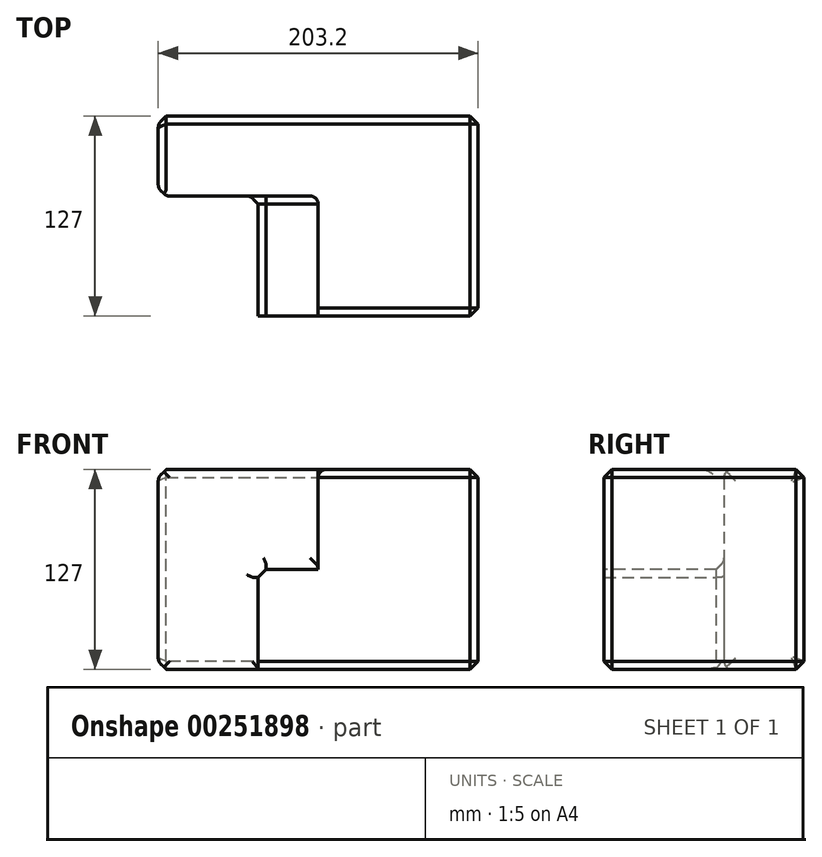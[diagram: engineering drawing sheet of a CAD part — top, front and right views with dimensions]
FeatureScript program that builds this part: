
annotation { "Feature Type Name" : "Feature", "Feature Type Description" : "" }
export const myFeature = defineFeature(function(context is Context, id is Id, definition is map)
    precondition{}
    {
        {
            var Q0;
            Q0=qCreatedBy(makeId("Front.planeOp"),FACE);
            var sketch = newSketch(context, id + "F0", { "sketchPlane" : qUnion([Q0])});
            skLineSegment(sketch, "E0.bottom", {"start": v(-101.6, 63.5) * mm, "end": v(101.6, 63.5) * mm});
            skLineSegment(sketch, "E0.top", {"start": v(-101.6, -63.5) * mm, "end": v(101.6, -63.5) * mm});
            skLineSegment(sketch, "E0.left", {"start": v(-101.6, 63.5) * mm, "end": v(-101.6, -63.5) * mm});
            skLineSegment(sketch, "E0.right", {"start": v(101.6, 63.5) * mm, "end": v(101.6, -63.5) * mm});
            skPoint(sketch, "E0.middle", {"position": v(0, 0) * mm});
            skSolve(sketch);
        }
        {
            var Q0;
            Q0 = qSketchRegion(id + "F0", true);
            extrude(context, id + "F1", {"entities" : qUnion([Q0]), "depth" : 127 * mm});
        }
        {
            var Q0;
            Q0=makeQuery(id+"F1.opExtrude","CAP_FACE",FACE,{"disambiguationData":[OSD([sQuery(id+"F0.wireOp",EDGE,"E0.bottom"),sQuery(id+"F0.wireOp",EDGE,"E0.top"),sQuery(id+"F0.wireOp",EDGE,"E0.left"),sQuery(id+"F0.wireOp",EDGE,"E0.right")])],"isStart":false});
            var sketch = newSketch(context, id + "F2", { "sketchPlane" : qUnion([Q0])});
            skLineSegment(sketch, "E1", {"start": v(-101.6, -63.5) * mm, "end": v(-101.6, 63.5) * mm});
            skLineSegment(sketch, "E2", {"start": v(-101.6, 63.5) * mm, "end": v(0, 63.5) * mm});
            skLineSegment(sketch, "E3", {"start": v(0, 63.5) * mm, "end": v(0, 0) * mm});
            skLineSegment(sketch, "E4", {"start": v(0, 0) * mm, "end": v(-38.1, 0) * mm});
            skLineSegment(sketch, "E5", {"start": v(-38.1, 0) * mm, "end": v(-38.1, -63.5) * mm});
            skLineSegment(sketch, "E6", {"start": v(-38.1, -63.5) * mm, "end": v(-101.6, -63.5) * mm});
            skSolve(sketch);
        }
        {
            var Q0;
            Q0=makeQuery(id+"F2.imprint","IMPRINT",FACE,{"disambiguationData":[TD([[makeQuery(id+"F2.imprint","IMPRINT",EDGE,{"derivedFrom":sQuery(id+"F2.wireOp",EDGE,"E1")}),1.0]])]});
            var sketch = newSketch(context, id + "F3", { "sketchPlane" : qUnion([Q0])});
            skSolve(sketch);
        }
        {
            var Q0;
            Q0 = qSketchRegion(id + "F3", true);
            var Q1;
            Q1=makeQuery(id+"F2.imprint","IMPRINT",FACE,{"disambiguationData":[TD([[makeQuery(id+"F2.imprint","IMPRINT",EDGE,{"derivedFrom":sQuery(id+"F2.wireOp",EDGE,"E1")}),1.0]])]});
            extrude(context, id + "F4", {"entities" : qUnion([Q0, Q1]), "operationType" : NewBodyOperationType.REMOVE, "oppositeDirection" : true, "depth" : 76.2 * mm});
        }
        {
            var Q0;
            Q0=makeQuery(id+"F4.boolean.opBoolean","COPY",EDGE,{"derivedFrom":makeQuery(id+"F4.opExtrude","SWEPT_EDGE",EDGE,{"disambiguationData":[OSD([sQuery(id+"F0.wireOp",EDGE,"E0.bottom"),sQuery(id+"F2.wireOp",EDGE,"E2"),sQuery(id+"F2.wireOp",EDGE,"E3")])]})});
            var Q1;
            Q1=makeQuery(id+"F4.boolean.opBoolean","COPY",EDGE,{"derivedFrom":makeQuery(id+"F4.opExtrude","CAP_EDGE",EDGE,{"disambiguationData":[OSD([sQuery(id+"F2.wireOp",EDGE,"E3")])],"isStart":true})});
            var Q2;
            Q2=makeQuery(id+"F4.boolean.opBoolean","COPY",EDGE,{"derivedFrom":makeQuery(id+"F4.opExtrude","SWEPT_EDGE",EDGE,{"disambiguationData":[OSD([sQuery(id+"F2.wireOp",EDGE,"E4"),sQuery(id+"F2.wireOp",EDGE,"E5")])]})});
            var Q3;
            Q3=makeQuery(id+"F4.boolean.opBoolean","COPY",EDGE,{"derivedFrom":makeQuery(id+"F4.opExtrude","CAP_EDGE",EDGE,{"disambiguationData":[OSD([sQuery(id+"F2.wireOp",EDGE,"E4")])],"isStart":true})});
            var Q4;
            Q4=makeQuery(id+"F4.boolean.opBoolean","COPY",EDGE,{"derivedFrom":makeQuery(id+"F4.opExtrude","CAP_EDGE",EDGE,{"disambiguationData":[OSD([sQuery(id+"F2.wireOp",EDGE,"E5")])],"isStart":false})});
            var Q5;
            Q5=makeQuery(id+"F4.boolean.opBoolean","COPY",EDGE,{"derivedFrom":makeQuery(id+"F4.opExtrude","CAP_EDGE",EDGE,{"disambiguationData":[OSD([sQuery(id+"F2.wireOp",EDGE,"E5")])],"isStart":true})});
            var Q6;
            Q6=makeQuery(id+"F4.boolean.opBoolean","COPY",EDGE,{"derivedFrom":makeQuery(id+"F4.opExtrude","SWEPT_EDGE",EDGE,{"disambiguationData":[OSD([sQuery(id+"F0.wireOp",EDGE,"E0.top"),sQuery(id+"F2.wireOp",EDGE,"E5"),sQuery(id+"F2.wireOp",EDGE,"E6")])]})});
            var Q7;
            Q7=makeQuery(id+"F1.opExtrude","CAP_EDGE",EDGE,{"disambiguationData":[OSD([sQuery(id+"F0.wireOp",EDGE,"E0.top")])],"isStart":false});
            var Q8;
            Q8=makeQuery(id+"F1.opExtrude","CAP_EDGE",EDGE,{"disambiguationData":[OSD([sQuery(id+"F0.wireOp",EDGE,"E0.right")])],"isStart":false});
            var Q9;
            Q9=makeQuery(id+"F1.opExtrude","CAP_EDGE",EDGE,{"disambiguationData":[OSD([sQuery(id+"F0.wireOp",EDGE,"E0.bottom")])],"isStart":false});
            var Q10;
            Q10=makeQuery(id+"F1.opExtrude","SWEPT_EDGE",EDGE,{"disambiguationData":[OSD([sQuery(id+"F0.wireOp",EDGE,"E0.bottom"),sQuery(id+"F0.wireOp",EDGE,"E0.right")])]});
            var Q11;
            Q11=makeQuery(id+"F1.opExtrude","SWEPT_EDGE",EDGE,{"disambiguationData":[OSD([sQuery(id+"F0.wireOp",EDGE,"E0.top"),sQuery(id+"F0.wireOp",EDGE,"E0.right")])]});
            var Q12;
            Q12=makeQuery(id+"F1.opExtrude","CAP_EDGE",EDGE,{"disambiguationData":[OSD([sQuery(id+"F0.wireOp",EDGE,"E0.right")])],"isStart":true});
            var Q13;
            Q13=makeQuery(id+"F1.opExtrude","CAP_EDGE",EDGE,{"disambiguationData":[OSD([sQuery(id+"F0.wireOp",EDGE,"E0.bottom")])],"isStart":true});
            var Q14;
            Q14=makeQuery(id+"F1.opExtrude","CAP_EDGE",EDGE,{"disambiguationData":[OSD([sQuery(id+"F0.wireOp",EDGE,"E0.top")])],"isStart":true});
            chamfer(context, id + "F5", {"entities" : qUnion([Q0, Q1, Q2, Q3, Q4, Q5, Q6, Q7, Q8, Q9, Q10, Q11, Q12, Q13, Q14]), "width" : 5.08 * mm, "tangentPropagation" : true});
        }
        {
            var Q0;
            Q0=makeQuery(id+"F1.opExtrude","SWEPT_EDGE",EDGE,{"disambiguationData":[OSD([sQuery(id+"F0.wireOp",EDGE,"E0.top"),sQuery(id+"F0.wireOp",EDGE,"E0.left")])]});
            var Q1;
            Q1=makeQuery(id+"F1.opExtrude","SWEPT_FACE",FACE,{"disambiguationData":[OSD([sQuery(id+"F0.wireOp",EDGE,"E0.left")])]});
            chamfer(context, id + "F6", {"entities" : qUnion([Q0, Q1]), "width" : 5.08 * mm, "tangentPropagation" : true});
        }
        {
            var Q0;
            {var subQ0=sQuery(id+"F0.wireOp",EDGE,"E0.left");Q0=makeQuery(id+"F6.opChamfer","BLEND_EDGE",EDGE,{"blendedFrom":[makeQuery(id+"F1.opExtrude","SWEPT_EDGE",EDGE,{"disambiguationData":[OSD([sQuery(id+"F0.wireOp",EDGE,"E0.top"),subQ0])]}),makeQuery(id+"F1.opExtrude","SWEPT_FACE",FACE,{"disambiguationData":[OSD([subQ0])]})],"blendedInto":[makeQuery(id+"F1.opExtrude","SWEPT_FACE",FACE,{"disambiguationData":[OSD([subQ0])]})]});}
            var Q1;
            Q1=makeQuery(id+"F4.boolean.opBoolean","COPY",FACE,{"derivedFrom":makeQuery(id+"F4.opExtrude","CAP_FACE",FACE,{"disambiguationData":[OSD([sQuery(id+"F2.wireOp",EDGE,"E1"),sQuery(id+"F2.wireOp",EDGE,"E2"),sQuery(id+"F2.wireOp",EDGE,"E3"),sQuery(id+"F2.wireOp",EDGE,"E4"),sQuery(id+"F2.wireOp",EDGE,"E5"),sQuery(id+"F2.wireOp",EDGE,"E6")])],"isStart":false})});
            var Q2;
            Q2=makeQuery(id+"F1.opExtrude","SWEPT_FACE",FACE,{"disambiguationData":[OSD([sQuery(id+"F0.wireOp",EDGE,"E0.left")])]});
            fillet(context, id + "F7", {"entities" : qUnion([Q0, Q1, Q2]), "radius" : 5.08 * mm, "tangentPropagation" : true, "allowEdgeOverflow" : false});
        }
    });
